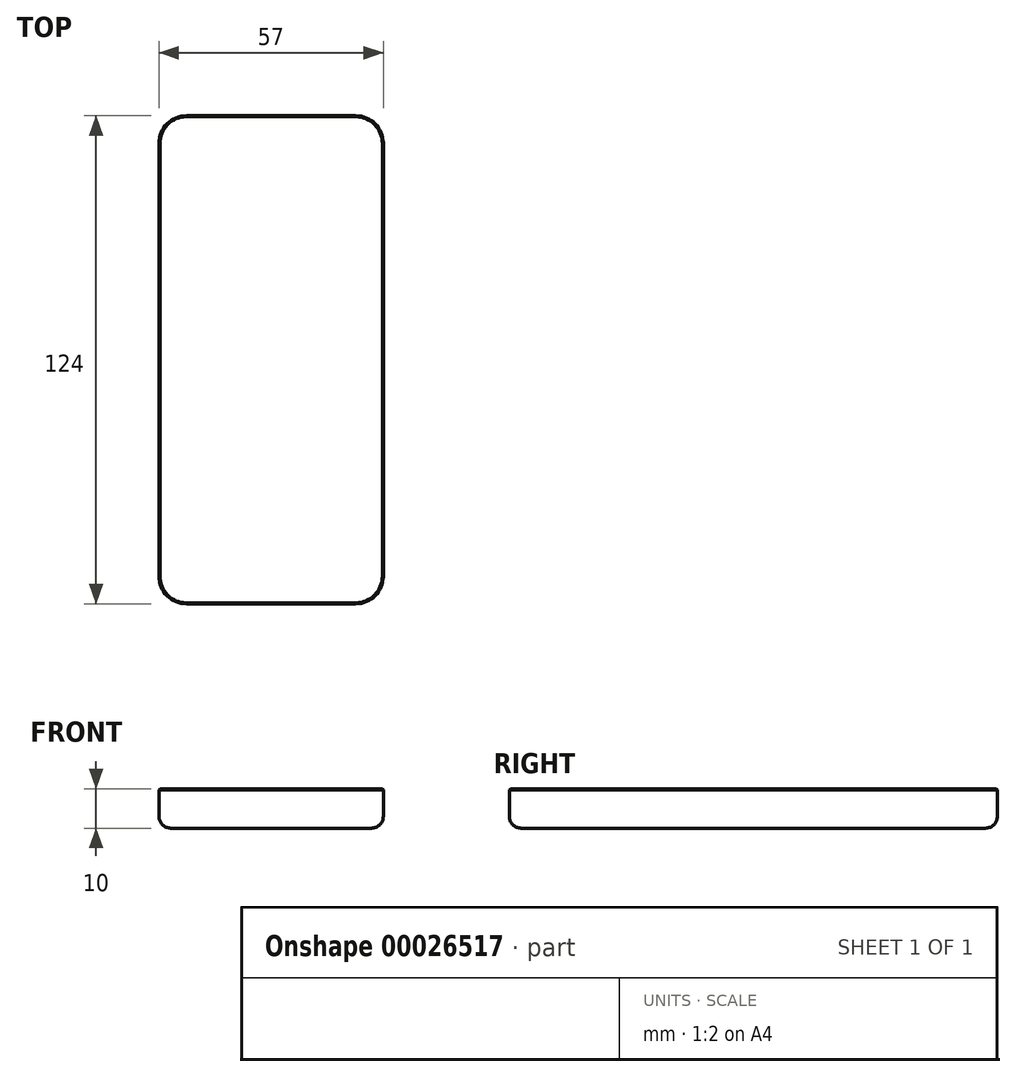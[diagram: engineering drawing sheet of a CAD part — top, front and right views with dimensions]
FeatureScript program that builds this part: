
annotation { "Feature Type Name" : "Feature", "Feature Type Description" : "" }
export const myFeature = defineFeature(function(context is Context, id is Id, definition is map)
    precondition{}
    {
        {
            var Q0;
            Q0=qCreatedBy(makeId("Top.planeOp"),FACE);
            var sketch = newSketch(context, id + "F0", { "sketchPlane" : qUnion([Q0])});
            skLineSegment(sketch, "E0.bottom", {"start": v(-68.12, -78.21) * mm, "end": v(-11.12, -78.21) * mm});
            skLineSegment(sketch, "E0.top", {"start": v(-68.12, 45.79) * mm, "end": v(-11.12, 45.79) * mm});
            skLineSegment(sketch, "E0.left", {"start": v(-68.12, -78.21) * mm, "end": v(-68.12, 45.79) * mm});
            skLineSegment(sketch, "E0.right", {"start": v(-11.12, -78.21) * mm, "end": v(-11.12, 45.79) * mm});
            skSolve(sketch);
        }
        {
            var Q0;
            Q0=makeQuery(id+"F0.imprint","IMPRINT",FACE,{"disambiguationData":[TD([[makeQuery(id+"F0.imprint","IMPRINT",EDGE,{"derivedFrom":sQuery(id+"F0.wireOp",EDGE,"E0.bottom")}),1.0]])]});
            extrude(context, id + "F1", {"entities" : qUnion([Q0]), "depth" : 10 * mm});
        }
        {
            var Q0;
            Q0=makeQuery(id+"F1.opExtrude","SWEPT_EDGE",EDGE,{"disambiguationData":[OSD([sQuery(id+"F0.wireOp",EDGE,"E0.bottom"),sQuery(id+"F0.wireOp",EDGE,"E0.right")])]});
            var Q1;
            Q1=makeQuery(id+"F1.opExtrude","SWEPT_EDGE",EDGE,{"disambiguationData":[OSD([sQuery(id+"F0.wireOp",EDGE,"E0.top"),sQuery(id+"F0.wireOp",EDGE,"E0.right")])]});
            var Q2;
            Q2=makeQuery(id+"F1.opExtrude","SWEPT_EDGE",EDGE,{"disambiguationData":[OSD([sQuery(id+"F0.wireOp",EDGE,"E0.bottom"),sQuery(id+"F0.wireOp",EDGE,"E0.left")])]});
            var Q3;
            Q3=makeQuery(id+"F1.opExtrude","SWEPT_EDGE",EDGE,{"disambiguationData":[OSD([sQuery(id+"F0.wireOp",EDGE,"E0.top"),sQuery(id+"F0.wireOp",EDGE,"E0.left")])]});
            fillet(context, id + "F2", {"entities" : qUnion([Q0, Q1, Q2, Q3]), "radius" : 7 * mm, "tangentPropagation" : true, "allowEdgeOverflow" : false});
        }
        {
            var Q0;
            Q0=makeQuery(id+"F1.opExtrude","CAP_FACE",FACE,{"disambiguationData":[OSD([sQuery(id+"F0.wireOp",EDGE,"E0.bottom"),sQuery(id+"F0.wireOp",EDGE,"E0.top"),sQuery(id+"F0.wireOp",EDGE,"E0.left"),sQuery(id+"F0.wireOp",EDGE,"E0.right")])],"isStart":true});
            fillet(context, id + "F3", {"entities" : qUnion([Q0]), "radius" : 3 * mm, "tangentPropagation" : true, "allowEdgeOverflow" : false});
        }
        {
            var Q0;
            Q0=makeQuery(id+"F1.opExtrude","CAP_FACE",FACE,{"disambiguationData":[OSD([sQuery(id+"F0.wireOp",EDGE,"E0.bottom"),sQuery(id+"F0.wireOp",EDGE,"E0.top"),sQuery(id+"F0.wireOp",EDGE,"E0.left"),sQuery(id+"F0.wireOp",EDGE,"E0.right")])],"isStart":false});
            chamfer(context, id + "F4", {"entities" : qUnion([Q0]), "width" : 0.25 * mm, "tangentPropagation" : true});
        }
    });
